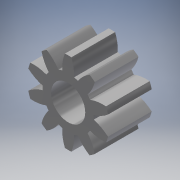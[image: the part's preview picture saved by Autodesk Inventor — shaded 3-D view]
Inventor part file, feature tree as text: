
AUTODESK INVENTOR PART (.ipt)
format: ipt  version: 2019 (Build 230136000, 136)  size: 196,096 bytes
history: native  units: mm (DEFAULTED — no unit token found)
features: plane x3, other x3, sketch x3, extrude x1, hole x1
ambient origin geometry x8: Origin, YZ Plane, XZ Plane, XY Plane, X Axis, Y Axis, Z Axis, Center Point
bodies: Solid1 (feature_tree)
feature tree (11):
  extrude  "Extrusion1"  Depth=3.2mm TaperAngle=0.0deg
  plane  "Work Plane2"
  plane  "Work Plane8"
  plane  "Work Plane9"
  other  "Przekładnia walcowa"
  hole  "Otwór1"  [1 undecoded]
  sketch  "Sketch1"  dims[d0=6.0mm d1=3.2mm d2=0.0mm]
  sketch  "Sketch2"  dims[d3=5.0mm d4=10.0mm d5=0.0mm d16=10.0mm d17=0.0mm d34=3.141593mm d39=0.0mm d41=0.0mm d43=10.0mm d46=10.0mm d47=0.0mm d48=0.0mm d49=2.5mm d50=6.0mm d51=4.0mm d52=2.0mm d53=90.0deg d54=8.0mm d55=20.594885mm]
  other  "Srf1"
  sketch  "Szkic3"
  other  "Średnica podziałowa"
note: 1 required parameter value undecoded (feature->parameter linkage not recoverable at this tier; creation-order binding heuristic only, values carry confidence <= 0.55)
